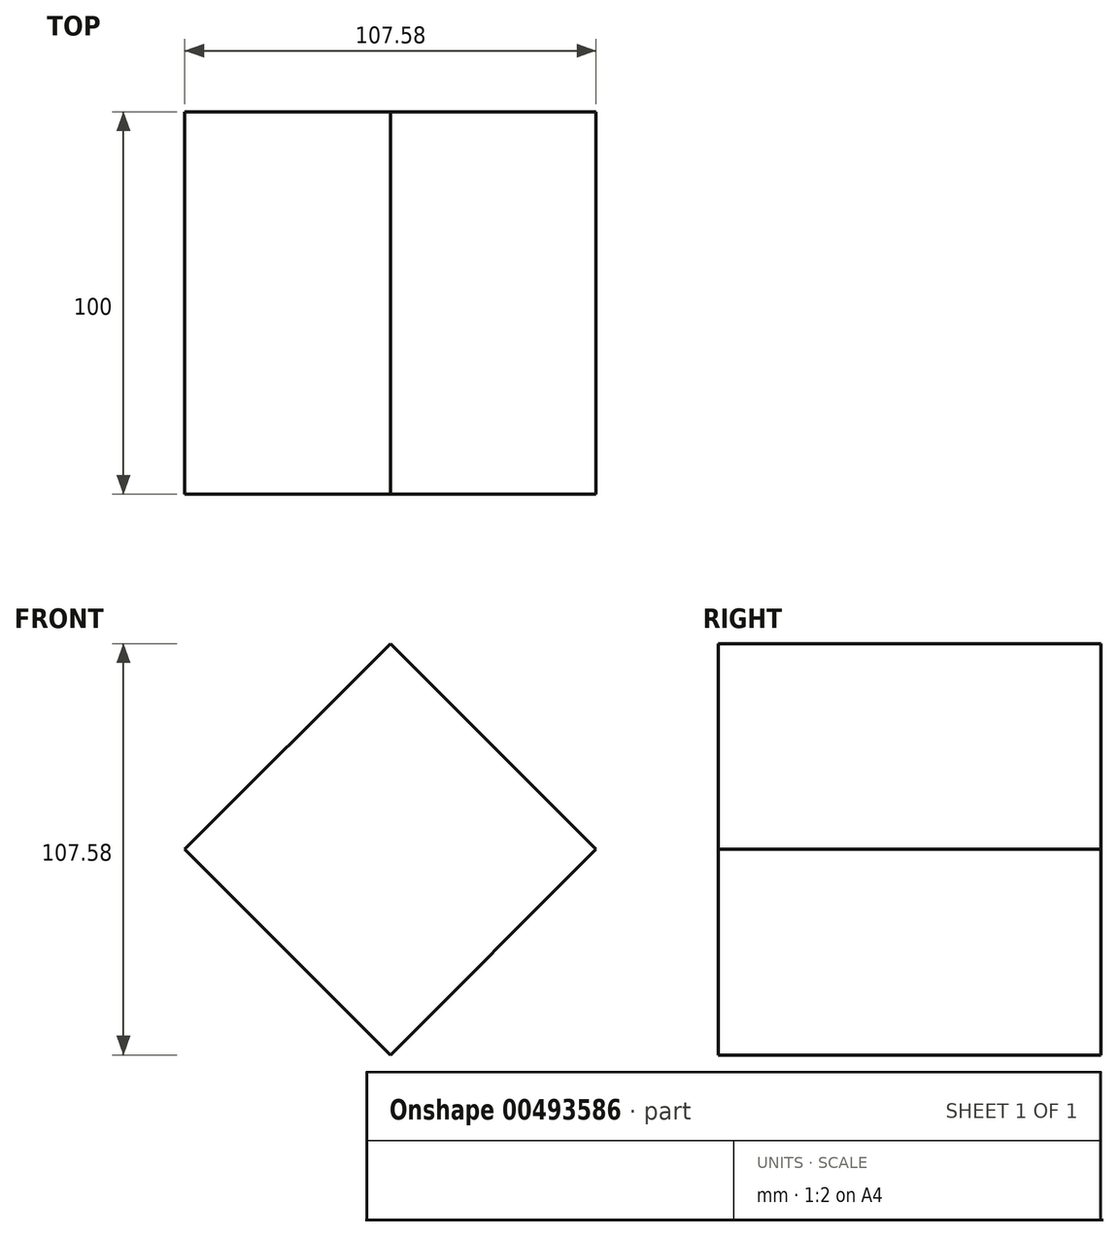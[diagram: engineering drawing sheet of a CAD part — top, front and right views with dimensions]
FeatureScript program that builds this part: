
annotation { "Feature Type Name" : "Feature", "Feature Type Description" : "" }
export const myFeature = defineFeature(function(context is Context, id is Id, definition is map)
    precondition{}
    {
        {
            var Q0;
            Q0=qCreatedBy(makeId("Front.planeOp"),FACE);
            var sketch = newSketch(context, id + "F0", { "sketchPlane" : qUnion([Q0])});
            skCircle(sketch, "E0.cCircle", {"center": v(0, 0) * mm, "radius": 53.8 * mm, "construction": true});
            skLineSegment(sketch, "E0.0", {"start": v(0, -53.8) * mm, "end": v(-53.8, 0) * mm});
            skLineSegment(sketch, "E0.1", {"start": v(-53.8, 0) * mm, "end": v(0, 53.8) * mm});
            skLineSegment(sketch, "E0.2", {"start": v(0, 53.8) * mm, "end": v(53.8, 0) * mm});
            skLineSegment(sketch, "E0.3", {"start": v(53.8, 0) * mm, "end": v(0, -53.8) * mm});
            skSolve(sketch);
        }
        {
            var Q0;
            Q0=makeQuery(id+"F0.imprint","IMPRINT",FACE,{"disambiguationData":[TD([[makeQuery(id+"F0.imprint","IMPRINT",EDGE,{"derivedFrom":sQuery(id+"F0.wireOp",EDGE,"E0.0")}),-1.0]])]});
            extrude(context, id + "F1", {"entities" : qUnion([Q0]), "endBound" : BoundingType.SYMMETRIC, "depth" : 100 * mm});
        }
    });
